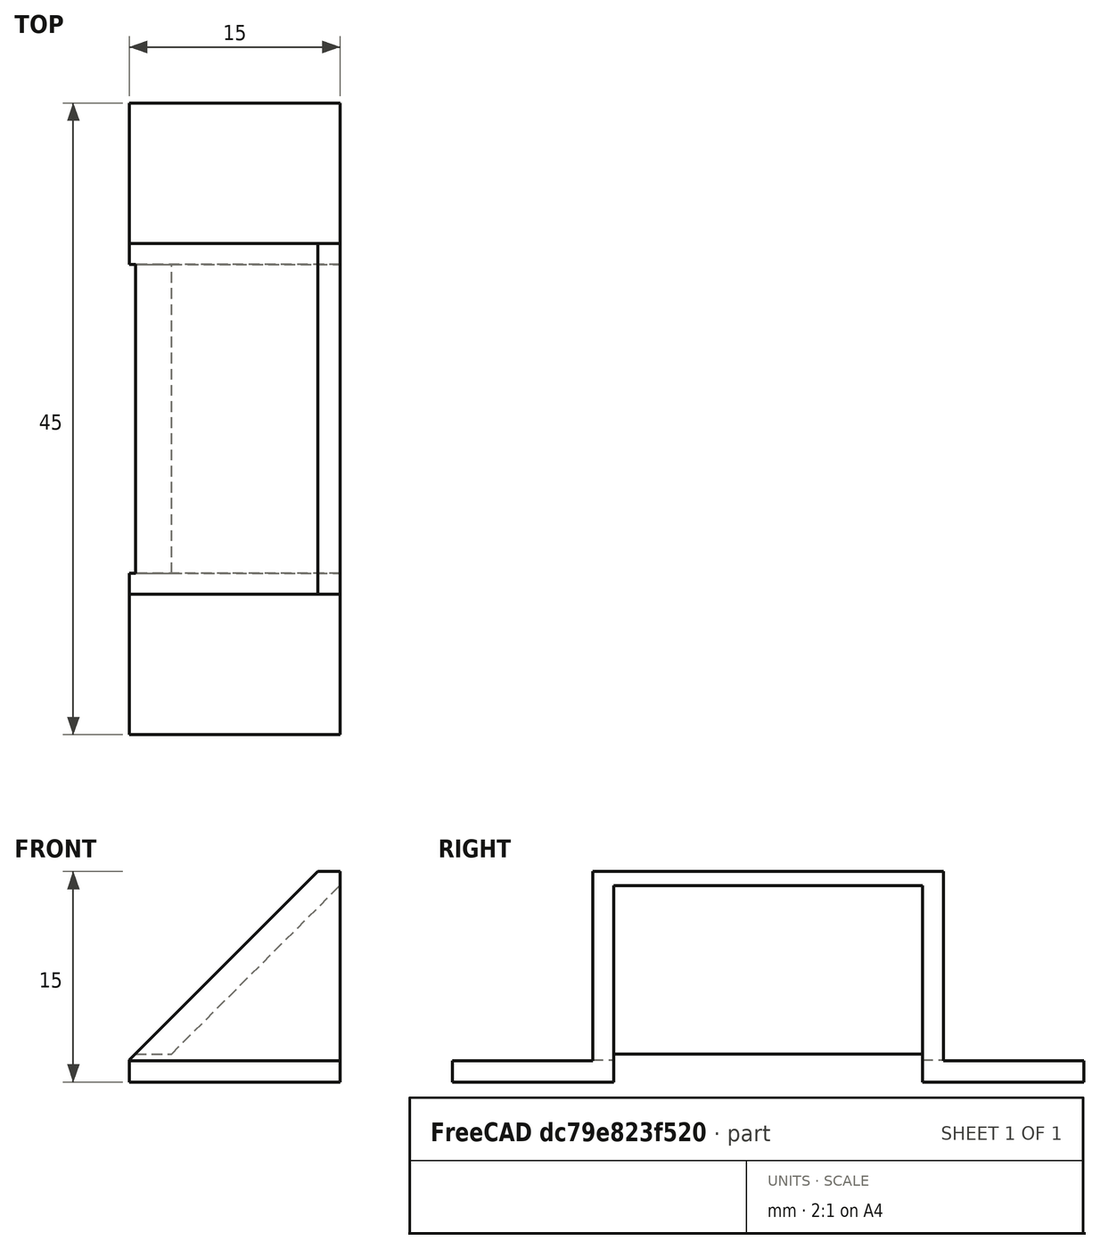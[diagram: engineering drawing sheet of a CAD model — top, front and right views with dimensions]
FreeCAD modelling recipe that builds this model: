
FCSTD DOCUMENT
Label: MirrorMount
License: CC-BY 3.0
LicenseURL: http://creativecommons.org/licenses/by/3.0/
objects: Part::Box×6, Part::MultiFuse×2, Part::Cut×1
note: 9 computed .brp shape members not serialized (recipe doc carries the construction recipe); baked Part::Feature solids carry a one-line shape summary decoded from their .brp

FEATURE [Part::Box] Box
  Height = 15
  Length = 15
  Width = 25
FEATURE [Part::Box] Box001
  Height = 1.5
  Length = 15
  Placement = pos=(0,25,0) rot=(0,0,1;0rad)
  Width = 10
FEATURE [Part::Box] Box001001  label="Box002"
  Height = 1.5
  Length = 15
  Placement = pos=(0,-10,0) rot=(0,0,1;0rad)
  Width = 10
FEATURE [Part::Box] Box001002  label="Box003"
  Height = 20
  Length = 10
  Placement = pos=(1,1.5,0) rot=(0,1,0;0.785397rad)
  Width = 22
FEATURE [Part::Box] Box001002001  label="Box004"
  Height = 22
  Length = 10
  Placement = pos=(-8.71,-1,7) rot=(0,1,0;0.785397rad)
  Width = 27
FEATURE [Part::Box] Box001002002  label="Box005"
  Height = 5
  Length = 10
  Placement = pos=(-3,1.5,-3) rot=(0,0,1;0rad)
  Width = 22
FEATURE [Part::MultiFuse] Fusion
  Shapes = -> [Box001002001,Box001002002,Box001002]
FEATURE [Part::Cut] Cut
  Base = -> Box
  Tool = -> Fusion
FEATURE [Part::MultiFuse] Fusion001  label="MirrorMount"
  Shapes = -> [Box001,Cut,Box001001]
